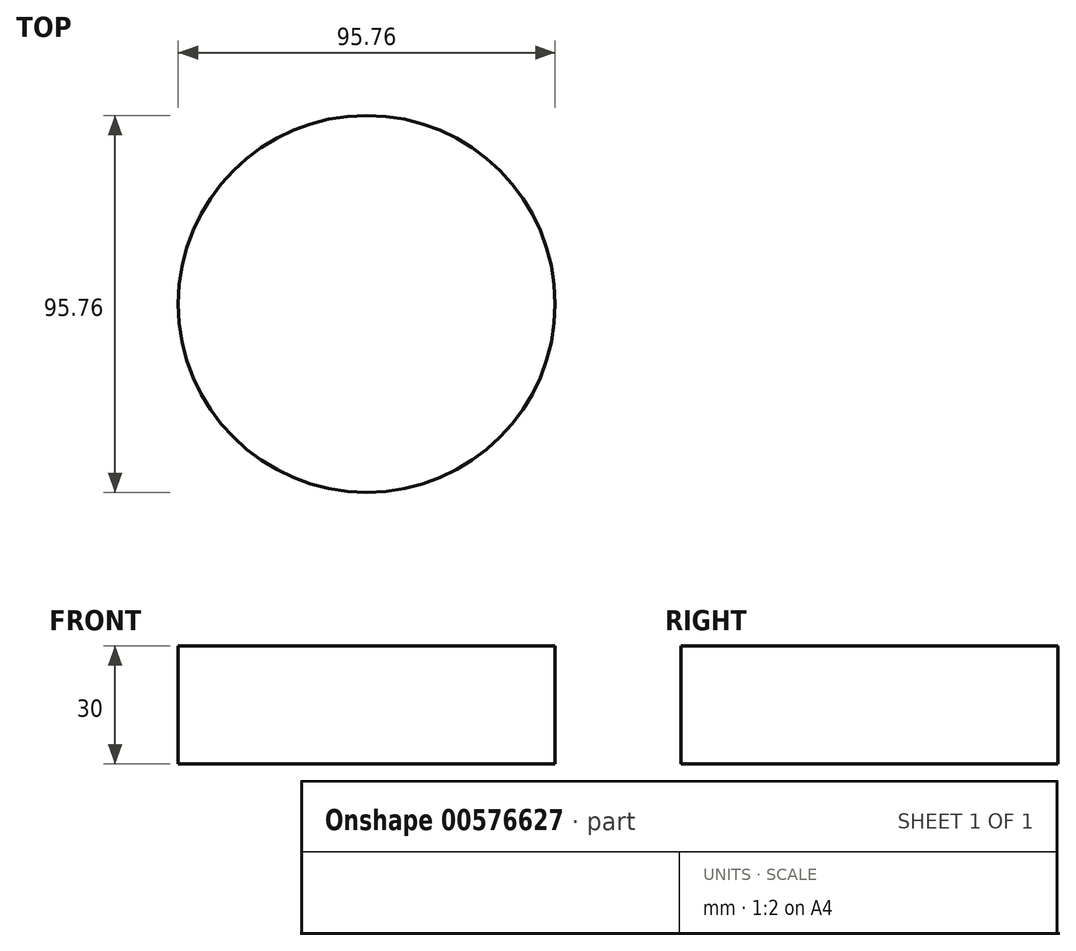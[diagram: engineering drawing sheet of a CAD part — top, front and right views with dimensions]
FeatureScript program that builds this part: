
annotation { "Feature Type Name" : "Feature", "Feature Type Description" : "" }
export const myFeature = defineFeature(function(context is Context, id is Id, definition is map)
    precondition{}
    {
        {
            var Q0;
            Q0=qCreatedBy(makeId("Top.planeOp"),FACE);
            var sketch = newSketch(context, id + "F0", { "sketchPlane" : qUnion([Q0])});
            skCircle(sketch, "E0", {"center": v(-1.47, -8.31) * mm, "radius": 47.88 * mm});
            skSolve(sketch);
        }
        {
            var Q0;
            Q0=makeQuery(id+"F0.imprint","IMPRINT",FACE,{"disambiguationData":[TD([[makeQuery(id+"F0.imprint","IMPRINT",EDGE,{"derivedFrom":sQuery(id+"F0.wireOp",EDGE,"E0")}),1.0]])]});
            extrude(context, id + "F1", {"entities" : qUnion([Q0]), "depth" : 30 * mm, "offsetDistance" : 25 * mm});
        }
    });
